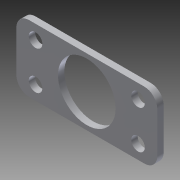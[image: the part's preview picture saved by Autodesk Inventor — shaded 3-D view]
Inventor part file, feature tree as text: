
AUTODESK INVENTOR PART (.ipt)
format: ipt  version: 2014 SP1 (Build 180222100, 222)  size: 118,272 bytes
history: native  units: in
note: dims shown in document units (in); Inventor stores cm internally (conversion verified against a paired STEP export)
features: reference x7, extrude x1, fillet x1, sketch x1
ambient origin geometry x8: Origin, YZ Plane, XZ Plane, XY Plane, X Axis, Y Axis, Z Axis, Center Point
bodies: Solid1 (feature_tree)
feature tree (10):
  extrude  "Extrusion1"  Depth=0.25in
  fillet  "Fillet1"  Radius=0.375in
  sketch  "Sketch1"  dims[d0=1.3in d1=0.375in d2=0.375in d3=0.05in d4=0.125in d5=0.0in d6=0.25in]
  reference  "Reference1"
  reference  "Reference2"
  reference  "Reference3"
  reference  "Reference4"
  reference  "Reference5"
  reference  "Reference6"
  reference  "Reference7"
